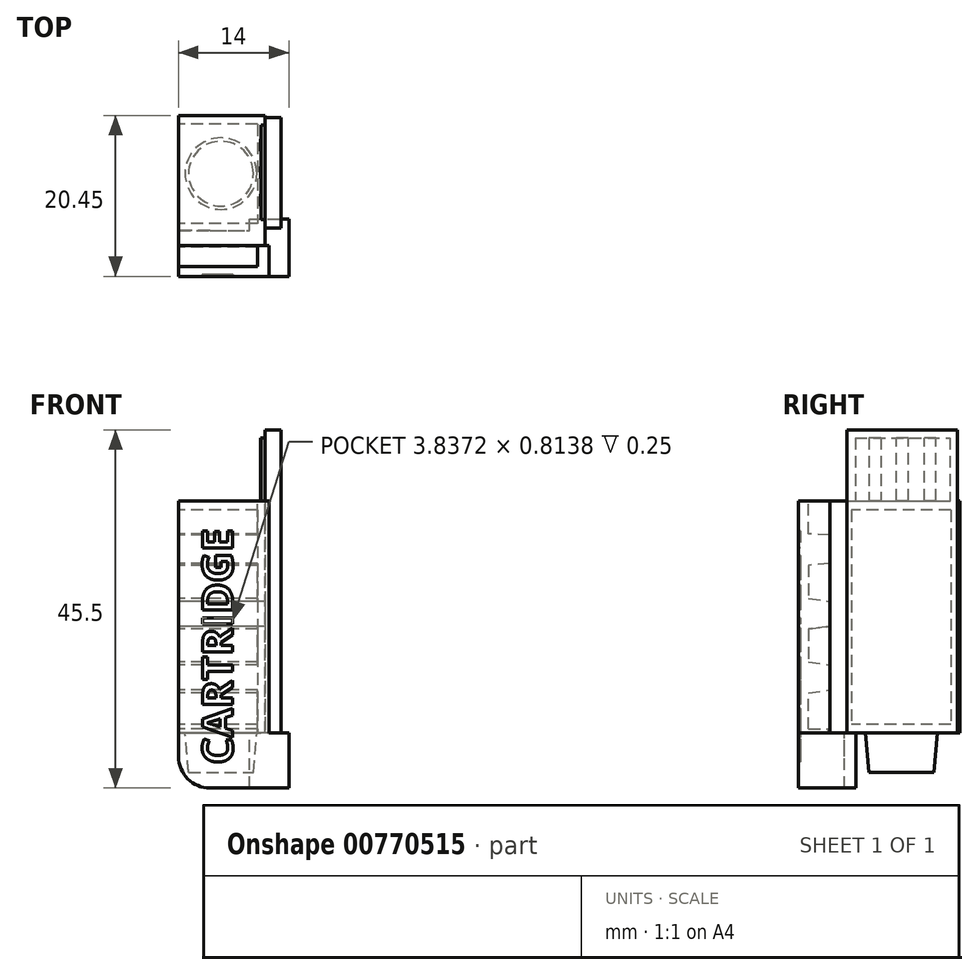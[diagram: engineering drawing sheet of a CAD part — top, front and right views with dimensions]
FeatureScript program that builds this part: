
annotation { "Feature Type Name" : "Feature", "Feature Type Description" : "" }
export const myFeature = defineFeature(function(context is Context, id is Id, definition is map)
    precondition{}
    {
        {
            var Q0;
            Q0=qCreatedBy(makeId("Right.planeOp"),FACE);
            var sketch = newSketch(context, id + "F0", { "sketchPlane" : qUnion([Q0])});
            skLineSegment(sketch, "E0", {"start": v(-7.8, 44.5) * mm, "end": v(-7.8, 0) * mm});
            skLineSegment(sketch, "E1", {"start": v(-7.8, 0) * mm, "end": v(0, 0) * mm});
            skLineSegment(sketch, "E2", {"start": v(0, 0) * mm, "end": v(0, 7) * mm});
            skLineSegment(sketch, "E3", {"start": v(0, 7) * mm, "end": v(-4.55, 7) * mm});
            skLineSegment(sketch, "E4", {"start": v(-5.05, 7.5) * mm, "end": v(-7.05, 7.5) * mm});
            skLineSegment(sketch, "E5", {"start": v(-7.05, 7.5) * mm, "end": v(-7.05, 12.1) * mm});
            skLineSegment(sketch, "E6", {"start": v(-4.35, 12.45) * mm, "end": v(-4.35, 15.65) * mm});
            skLineSegment(sketch, "E7", {"start": v(-7.05, 16) * mm, "end": v(-7.05, 20.2) * mm});
            skLineSegment(sketch, "E8", {"start": v(-4.35, 20.53) * mm, "end": v(-4.35, 23.73) * mm});
            skLineSegment(sketch, "E9", {"start": v(-7.05, 24.1) * mm, "end": v(-7.05, 28.3) * mm});
            skLineSegment(sketch, "E10", {"start": v(-7.05, 32.3) * mm, "end": v(-7.05, 36.5) * mm});
            skLineSegment(sketch, "E11", {"start": v(-7.05, 36.5) * mm, "end": v(-2.8, 36.5) * mm});
            skLineSegment(sketch, "E12", {"start": v(-4.55, 7) * mm, "end": v(-7.8, 7) * mm});
            skLineSegment(sketch, "E13", {"start": v(-5.05, 7.5) * mm, "end": v(-4.55, 7.5) * mm});
            skLineSegment(sketch, "E14", {"start": v(-4.55, 7.5) * mm, "end": v(-4.55, 7) * mm});
            skLineSegment(sketch, "E15", {"start": v(-2.8, 36.5) * mm, "end": v(-2.8, 44.5) * mm});
            skLineSegment(sketch, "E16", {"start": v(-2.8, 44.5) * mm, "end": v(-7.8, 44.5) * mm});
            skLineSegment(sketch, "E17", {"start": v(-4.35, 32.13) * mm, "end": v(-7.05, 32.3) * mm});
            skLineSegment(sketch, "E18", {"start": v(-4.35, 28.53) * mm, "end": v(-7.05, 28.3) * mm});
            skLineSegment(sketch, "E19", {"start": v(-4.35, 32.13) * mm, "end": v(-4.35, 28.53) * mm});
            skLineSegment(sketch, "E20", {"start": v(-7.05, 24.1) * mm, "end": v(-4.35, 23.73) * mm});
            skLineSegment(sketch, "E21", {"start": v(-7.05, 20.2) * mm, "end": v(-4.35, 20.53) * mm});
            skLineSegment(sketch, "E22", {"start": v(-7.05, 12.1) * mm, "end": v(-4.35, 12.45) * mm});
            skLineSegment(sketch, "E23", {"start": v(-4.35, 15.65) * mm, "end": v(-7.05, 16) * mm});
            skSolve(sketch);
        }
        {
            var Q0;
            Q0=makeQuery(id+"F0.imprint","IMPRINT",FACE,{"disambiguationData":[TD([[makeQuery(id+"F0.imprint","IMPRINT",EDGE,{"derivedFrom":sQuery(id+"F0.wireOp",EDGE,"E4")}),1.0]])]});
            extrude(context, id + "F1", {"entities" : qUnion([Q0]), "depth" : 10 * mm, "offsetDistance" : 25 * mm});
        }
        {
            var Q0;
            {var subQ0=sQuery(id+"F0.wireOp",EDGE,"E1");Q0=makeQuery(id+"F0.imprint","IMPRINT",FACE,{"disambiguationData":[TD([[makeQuery(id+"F0.imprint","IMPRINT",EDGE,{"derivedFrom":subQ0}),1.0]])]});}
            extrude(context, id + "F2", {"entities" : qUnion([Q0]), "operationType" : NewBodyOperationType.ADD, "depth" : 14 * mm});
        }
        {
            var Q0;
            Q0=makeQuery(id+"F0.imprint","IMPRINT",FACE,{"disambiguationData":[TD([[makeQuery(id+"F0.imprint","IMPRINT",EDGE,{"derivedFrom":sQuery(id+"F0.wireOp",EDGE,"E4")}),1.0]])]});
            var sketch = newSketch(context, id + "F3", { "sketchPlane" : qUnion([Q0])});
            skLineSegment(sketch, "E24.bottom", {"start": v(-2.8, 44.5) * mm, "end": v(-7.8, 44.5) * mm});
            skLineSegment(sketch, "E24.top", {"start": v(-2.8, 0) * mm, "end": v(-7.8, 0) * mm});
            skLineSegment(sketch, "E24.left", {"start": v(-2.8, 44.5) * mm, "end": v(-2.8, 0) * mm});
            skLineSegment(sketch, "E24.right", {"start": v(-7.8, 44.5) * mm, "end": v(-7.8, 0) * mm});
            skSolve(sketch);
        }
        {
            var Q0;
            Q0=makeQuery(id+"F1.opExtrude","CAP_FACE",FACE,{"disambiguationData":[OSD([sQuery(id+"F0.wireOp",EDGE,"E0"),sQuery(id+"F0.wireOp",EDGE,"E4"),sQuery(id+"F0.wireOp",EDGE,"E5"),sQuery(id+"F0.wireOp",EDGE,"E6"),sQuery(id+"F0.wireOp",EDGE,"E7"),sQuery(id+"F0.wireOp",EDGE,"E8"),sQuery(id+"F0.wireOp",EDGE,"E9"),sQuery(id+"F0.wireOp",EDGE,"E10"),sQuery(id+"F0.wireOp",EDGE,"E11"),sQuery(id+"F0.wireOp",EDGE,"E12"),sQuery(id+"F0.wireOp",EDGE,"E13"),sQuery(id+"F0.wireOp",EDGE,"E14"),sQuery(id+"F0.wireOp",EDGE,"E15"),sQuery(id+"F0.wireOp",EDGE,"E16"),sQuery(id+"F0.wireOp",EDGE,"E17"),sQuery(id+"F0.wireOp",EDGE,"E18"),sQuery(id+"F0.wireOp",EDGE,"E19"),sQuery(id+"F0.wireOp",EDGE,"E20"),sQuery(id+"F0.wireOp",EDGE,"E21"),sQuery(id+"F0.wireOp",EDGE,"E22"),sQuery(id+"F0.wireOp",EDGE,"E23")])],"isStart":false});
            var sketch = newSketch(context, id + "F4", { "sketchPlane" : qUnion([Q0])});
            skLineSegment(sketch, "E25.bottom", {"start": v(-7.8, 44.5) * mm, "end": v(-4.35, 44.5) * mm});
            skLineSegment(sketch, "E25.top", {"start": v(-7.8, 7) * mm, "end": v(-4.35, 7) * mm});
            skLineSegment(sketch, "E25.left", {"start": v(-7.8, 44.5) * mm, "end": v(-7.8, 7) * mm});
            skLineSegment(sketch, "E25.right", {"start": v(-4.35, 44.5) * mm, "end": v(-4.35, 7) * mm});
            skSolve(sketch);
        }
        {
            var Q0;
            Q0=qSketchRegion(id+"F4",true);
            extrude(context, id + "F5", {"entities" : qUnion([Q0]), "operationType" : NewBodyOperationType.ADD, "depth" : 1.5 * mm, "offsetDistance" : 25 * mm});
        }
        {
            var Q0;
            Q0=makeQuery(id+"F1.opExtrude","CAP_EDGE",EDGE,{"disambiguationData":[OSD([sQuery(id+"F0.wireOp",EDGE,"E16")])],"isStart":true});
            var Q1;
            Q1=makeQuery(id+"F2.opExtrude","CAP_EDGE",EDGE,{"disambiguationData":[OSD([sQuery(id+"F0.wireOp",EDGE,"E1")])],"isStart":true});
            fillet(context, id + "F6", {"entities" : qUnion([Q0, Q1]), "radius" : 4 * mm, "tangentPropagation" : true, "allowEdgeOverflow" : false});
        }
        {
            var Q0;
            Q0=makeQuery(id+"F1.opExtrude","SWEPT_FACE",FACE,{"disambiguationData":[OSD([sQuery(id+"F0.wireOp",EDGE,"E15")])]});
            var sketch = newSketch(context, id + "F7", { "sketchPlane" : qUnion([Q0])});
            skLineSegment(sketch, "E26.bottom", {"start": v(-11.5, 36.5) * mm, "end": v(0, 36.5) * mm});
            skLineSegment(sketch, "E26.top", {"start": v(-11.5, 44.5) * mm, "end": v(0, 44.5) * mm});
            skLineSegment(sketch, "E26.left", {"start": v(0, 36.5) * mm, "end": v(0, 44.5) * mm});
            skLineSegment(sketch, "E26.right", {"start": v(-11.5, 36.5) * mm, "end": v(-11.5, 44.5) * mm});
            skSolve(sketch);
        }
        {
            var Q0;
            Q0=qSketchRegion(id+"F7",true);
            extrude(context, id + "F8", {"entities" : qUnion([Q0]), "operationType" : NewBodyOperationType.REMOVE, "oppositeDirection" : true, "depth" : 25 * mm, "offsetDistance" : 25 * mm});
        }
        {
            var Q0;
            Q0=makeQuery(id+"F2.opExtrude","CAP_FACE",FACE,{"disambiguationData":[OSD([sQuery(id+"F0.wireOp",EDGE,"E0"),sQuery(id+"F0.wireOp",EDGE,"E1"),sQuery(id+"F0.wireOp",EDGE,"E2"),sQuery(id+"F0.wireOp",EDGE,"E3"),sQuery(id+"F0.wireOp",EDGE,"E12")])],"isStart":false});
            var sketch = newSketch(context, id + "F9", { "sketchPlane" : qUnion([Q0])});
            skLineSegment(sketch, "E27.bottom", {"start": v(0, 0) * mm, "end": v(-1, 0) * mm});
            skLineSegment(sketch, "E27.top", {"start": v(0, 7) * mm, "end": v(-1, 7) * mm});
            skLineSegment(sketch, "E27.left", {"start": v(0, 0) * mm, "end": v(0, 7) * mm});
            skLineSegment(sketch, "E27.right", {"start": v(-1, 0) * mm, "end": v(-1, 7) * mm});
            skSolve(sketch);
        }
        {
            var Q0;
            Q0=qSketchRegion(id+"F9",true);
            extrude(context, id + "F10", {"entities" : qUnion([Q0]), "operationType" : NewBodyOperationType.REMOVE, "endBound" : BoundingType.THROUGH_ALL, "oppositeDirection" : true, "depth" : 25 * mm, "offsetDistance" : 25 * mm});
        }
        {
            var Q0;
            {var subQ0=sQuery(id+"F0.wireOp",EDGE,"E0");Q0=makeQuery(id+"F5.boolean.opBoolean","MERGE",FACE,{"derivedFrom":[makeQuery(id+"F2.boolean.opBoolean","MERGE",FACE,{"derivedFrom":[makeQuery(id+"F1.opExtrude","SWEPT_FACE",FACE,{"disambiguationData":[OSD([subQ0])]}),makeQuery(id+"F2.opExtrude","SWEPT_FACE",FACE,{"disambiguationData":[OSD([subQ0])]})]}),makeQuery(id+"F5.opExtrude","SWEPT_FACE",FACE,{"disambiguationData":[OSD([sQuery(id+"F4.wireOp",EDGE,"E25.left")])]})]});}
            var sketch = newSketch(context, id + "F11", { "sketchPlane" : qUnion([Q0])});
            skLineSegment(sketch, "E28", {"start": v(0, 36.5) * mm, "end": v(11.5, 36.5) * mm});
            skLineSegment(sketch, "E29", {"start": v(11.5, 36.5) * mm, "end": v(11.5, 7) * mm});
            skLineSegment(sketch, "E30", {"start": v(11.5, 7) * mm, "end": v(14, 7) * mm});
            skLineSegment(sketch, "E31", {"start": v(14, 7) * mm, "end": v(14, 0) * mm});
            skLineSegment(sketch, "E32", {"start": v(14, 0) * mm, "end": v(4, 0) * mm});
            skLineSegment(sketch, "E33", {"start": v(0, 4) * mm, "end": v(0, 36.5) * mm});
            skArc(sketch, "E34.filletArc", {"start": v(0, 4) * mm, "mid": v(1.17, 1.17) * mm, "end": v(4, 0) * mm});
            skSolve(sketch);
        }
        {
            var Q0;
            Q0=qSketchRegion(id+"F11",true);
            extrude(context, id + "F12", {"entities" : qUnion([Q0]), "operationType" : NewBodyOperationType.ADD, "depth" : 0.5 * mm, "offsetDistance" : 25 * mm});
        }
        {
            var Q0;
            Q0=makeQuery(id+"F10.boolean.opBoolean","COPY",FACE,{"derivedFrom":makeQuery(id+"F10.opExtrude","SWEPT_FACE",FACE,{"disambiguationData":[OSD([sQuery(id+"F9.wireOp",EDGE,"E27.right")])]})});
            var sketch = newSketch(context, id + "F13", { "sketchPlane" : qUnion([Q0])});
            skLineSegment(sketch, "E35.bottom", {"start": v(0, 0) * mm, "end": v(0, 7) * mm});
            skLineSegment(sketch, "E35.top", {"start": v(-9, 0) * mm, "end": v(-9, 7) * mm});
            skLineSegment(sketch, "E35.left", {"start": v(0, 0) * mm, "end": v(-9, 0) * mm});
            skLineSegment(sketch, "E35.right", {"start": v(0, 7) * mm, "end": v(-9, 7) * mm});
            skSolve(sketch);
        }
        {
            var Q0;
            Q0=qSketchRegion(id+"F13",true);
            extrude(context, id + "F14", {"entities" : qUnion([Q0]), "operationType" : NewBodyOperationType.REMOVE, "oppositeDirection" : true, "depth" : 1.5 * mm, "offsetDistance" : 25 * mm});
        }
        {
            var Q0;
            Q0=makeQuery(id+"F12.opExtrude","CAP_FACE",FACE,{"disambiguationData":[OSD([sQuery(id+"F11.wireOp",EDGE,"E28"),sQuery(id+"F11.wireOp",EDGE,"E29"),sQuery(id+"F11.wireOp",EDGE,"E30"),sQuery(id+"F11.wireOp",EDGE,"E31"),sQuery(id+"F11.wireOp",EDGE,"E32"),sQuery(id+"F11.wireOp",EDGE,"E33"),sQuery(id+"F11.wireOp",EDGE,"E34.filletArc")])],"isStart":false});
            var sketch = newSketch(context, id + "F15", { "sketchPlane" : qUnion([Q0])});
            skText(sketch, "E36", { "text": "CARTRIDGE", "fontName": "OpenSans-Bold.ttf"});
            const initialGuessF15  = {"E36": [0.00687, 0.003, 0, 1, 0.00387]};
            skSetInitialGuess(sketch, initialGuessF15);
            skSolve(sketch);
        }
        {
            var Q0;
            Q0=qSketchRegion(id+"F15",true);
            extrude(context, id + "F16", {"entities" : qUnion([Q0]), "operationType" : NewBodyOperationType.REMOVE, "oppositeDirection" : true, "depth" : 0.25 * mm, "offsetDistance" : 25 * mm});
        }
        {
            var Q0;
            Q0=qCreatedBy(makeId("Right.planeOp"),FACE);
            var sketch = newSketch(context, id + "F17", { "sketchPlane" : qUnion([Q0])});
            skLineSegment(sketch, "E37", {"start": v(-7.05, 36.5) * mm, "end": v(12.15, 36.5) * mm});
            skLineSegment(sketch, "E38", {"start": v(12.15, 36.5) * mm, "end": v(12.15, 7) * mm});
            skLineSegment(sketch, "E39", {"start": v(-7.05, 36.5) * mm, "end": v(-7.05, 32.3) * mm});
            skLineSegment(sketch, "E40", {"start": v(-7.05, 32.3) * mm, "end": v(-4.35, 32.13) * mm});
            skLineSegment(sketch, "E41", {"start": v(-4.35, 32.13) * mm, "end": v(-4.35, 28.53) * mm});
            skLineSegment(sketch, "E42", {"start": v(-4.35, 28.53) * mm, "end": v(-7.05, 28.3) * mm});
            skLineSegment(sketch, "E43", {"start": v(-7.05, 28.3) * mm, "end": v(-7.05, 24.1) * mm});
            skLineSegment(sketch, "E44", {"start": v(-7.05, 24.1) * mm, "end": v(-4.35, 23.73) * mm});
            skLineSegment(sketch, "E45", {"start": v(-4.35, 23.73) * mm, "end": v(-4.35, 20.53) * mm});
            skLineSegment(sketch, "E46", {"start": v(-4.35, 20.53) * mm, "end": v(-7.05, 20.2) * mm});
            skLineSegment(sketch, "E47", {"start": v(-7.05, 20.2) * mm, "end": v(-7.05, 16) * mm});
            skLineSegment(sketch, "E48", {"start": v(-7.05, 16) * mm, "end": v(-4.35, 15.65) * mm});
            skLineSegment(sketch, "E49", {"start": v(-4.35, 15.65) * mm, "end": v(-4.35, 12.45) * mm});
            skLineSegment(sketch, "E50", {"start": v(-4.35, 12.45) * mm, "end": v(-7.05, 12.1) * mm});
            skLineSegment(sketch, "E51", {"start": v(-7.05, 12.1) * mm, "end": v(-7.05, 7.5) * mm});
            skLineSegment(sketch, "E52", {"start": v(-4.35, 36.5) * mm, "end": v(-4.35, 7) * mm});
            skPoint(sketch, "E52.startSnap0", {"position": v(-4.35, 30.33) * mm});
            skLineSegment(sketch, "E53", {"start": v(-4.55, 7.5) * mm, "end": v(-4.55, 7) * mm});
            skLineSegment(sketch, "E54", {"start": v(-4.55, 7) * mm, "end": v(12.15, 7) * mm});
            skLineSegment(sketch, "E55", {"start": v(-4.55, 7.5) * mm, "end": v(-7.05, 7.5) * mm});
            skSolve(sketch);
        }
        {
            var Q0;
            {var subQ12=sQuery(id+"F17.wireOp",EDGE,"E38");Q0=makeQuery(id+"F17.imprint","IMPRINT",FACE,{"disambiguationData":[TD([[makeQuery(id+"F17.imprint","IMPRINT",EDGE,{"derivedFrom":subQ12}),-1.0]])]});}
            extrude(context, id + "F18", {"entities" : qUnion([Q0]), "depth" : 11 * mm, "offsetDistance" : 25 * mm});
        }
        {
            var Q0;
            {var subQ0=sQuery(id+"F17.wireOp",EDGE,"E39");Q0=makeQuery(id+"F17.imprint","IMPRINT",FACE,{"disambiguationData":[TD([[makeQuery(id+"F17.imprint","IMPRINT",EDGE,{"derivedFrom":subQ0}),1.0]])]});}
            var Q1;
            {var subQ0=sQuery(id+"F17.wireOp",EDGE,"E42");Q1=makeQuery(id+"F17.imprint","IMPRINT",FACE,{"disambiguationData":[TD([[makeQuery(id+"F17.imprint","IMPRINT",EDGE,{"derivedFrom":subQ0}),1.0]])]});}
            var Q2;
            {var subQ0=sQuery(id+"F17.wireOp",EDGE,"E47");Q2=makeQuery(id+"F17.imprint","IMPRINT",FACE,{"disambiguationData":[TD([[makeQuery(id+"F17.imprint","IMPRINT",EDGE,{"derivedFrom":subQ0}),1.0]])]});}
            var Q3;
            {var subQ2=sQuery(id+"F17.wireOp",EDGE,"E50");Q3=makeQuery(id+"F17.imprint","IMPRINT",FACE,{"disambiguationData":[TD([[makeQuery(id+"F17.imprint","IMPRINT",EDGE,{"derivedFrom":subQ2}),1.0]])]});}
            extrude(context, id + "F19", {"entities" : qUnion([Q0, Q1, Q2, Q3]), "depth" : 10 * mm, "offsetDistance" : 25 * mm});
        }
        {
            var Q0;
            Q0=makeQuery(id+"F18.opExtrude","SWEPT_FACE",FACE,{"disambiguationData":[OSD([sQuery(id+"F17.wireOp",EDGE,"E54")])]});
            var sketch = newSketch(context, id + "F20", { "sketchPlane" : qUnion([Q0])});
            skCircle(sketch, "E56", {"center": v(5.38, -4.76) * mm, "radius": 4.55 * mm});
            skSolve(sketch);
        }
        {
            var Q0;
            Q0=makeQuery(id+"F20.imprint","IMPRINT",FACE,{"disambiguationData":[TD([[makeQuery(id+"F20.imprint","IMPRINT",EDGE,{"derivedFrom":sQuery(id+"F20.wireOp",EDGE,"E56")}),1.0]])]});
            extrude(context, id + "F21", {"entities" : qUnion([Q0]), "depth" : 5 * mm, "offsetDistance" : 25 * mm, "hasDraft" : true, "draftAngle" : 5 * degree, "draftPullDirection" : true});
        }
        {
            var Q0;
            Q0=makeQuery(id+"F18.opExtrude","SWEPT_FACE",FACE,{"disambiguationData":[OSD([sQuery(id+"F17.wireOp",EDGE,"E37")])]});
            var sketch = newSketch(context, id + "F22", { "sketchPlane" : qUnion([Q0])});
            skLineSegment(sketch, "E57.bottom", {"start": v(11, 10.9) * mm, "end": v(10.5, 10.9) * mm});
            skLineSegment(sketch, "E57.top", {"start": v(11, -1.1) * mm, "end": v(10.5, -1.1) * mm});
            skLineSegment(sketch, "E57.left", {"start": v(11, 10.9) * mm, "end": v(11, -1.1) * mm});
            skLineSegment(sketch, "E57.right", {"start": v(10.5, 10.9) * mm, "end": v(10.5, -1.1) * mm});
            skSolve(sketch);
        }
        {
            var Q0;
            Q0=makeQuery(id+"F22.imprint","IMPRINT",FACE,{"disambiguationData":[TD([[makeQuery(id+"F22.imprint","IMPRINT",EDGE,{"derivedFrom":sQuery(id+"F22.wireOp",EDGE,"E57.bottom")}),1.0]])]});
            extrude(context, id + "F23", {"entities" : qUnion([Q0]), "depth" : 8 * mm, "offsetDistance" : 25 * mm});
        }
        {
            var Q0;
            Q0=makeQuery(id+"F23.opExtrude","SWEPT_FACE",FACE,{"disambiguationData":[OSD([sQuery(id+"F22.wireOp",EDGE,"E57.right")])]});
            var sketch = newSketch(context, id + "F24", { "sketchPlane" : qUnion([Q0])});
            skLineSegment(sketch, "E58.bottom", {"start": v(-0.65, 44.5) * mm, "end": v(-2.15, 44.5) * mm});
            skLineSegment(sketch, "E58.top", {"start": v(-0.65, 36.5) * mm, "end": v(-2.15, 36.5) * mm});
            skLineSegment(sketch, "E58.left", {"start": v(-0.65, 44.5) * mm, "end": v(-0.65, 36.5) * mm});
            skLineSegment(sketch, "E58.right", {"start": v(-2.15, 44.5) * mm, "end": v(-2.15, 36.5) * mm});
            skLineSegment(sketch, "E59.bottom", {"start": v(-4.15, 36.5) * mm, "end": v(-5.65, 36.5) * mm});
            skLineSegment(sketch, "E59.top", {"start": v(-4.15, 44.5) * mm, "end": v(-5.65, 44.5) * mm});
            skLineSegment(sketch, "E59.left", {"start": v(-4.15, 36.5) * mm, "end": v(-4.15, 44.5) * mm});
            skLineSegment(sketch, "E59.right", {"start": v(-5.65, 36.5) * mm, "end": v(-5.65, 44.5) * mm});
            skLineSegment(sketch, "E60.bottom", {"start": v(-7.65, 36.5) * mm, "end": v(-9.15, 36.5) * mm});
            skLineSegment(sketch, "E60.top", {"start": v(-7.65, 44.5) * mm, "end": v(-9.15, 44.5) * mm});
            skLineSegment(sketch, "E60.left", {"start": v(-7.65, 36.5) * mm, "end": v(-7.65, 44.5) * mm});
            skLineSegment(sketch, "E60.right", {"start": v(-9.15, 36.5) * mm, "end": v(-9.15, 44.5) * mm});
            skSolve(sketch);
        }
        {
            var Q0;
            Q0 = qSketchRegion(id + "F24", true);
            extrude(context, id + "F25", {"entities" : qUnion([Q0]), "depth" : 0.1 * mm, "offsetDistance" : 25 * mm});
        }
        {
            var Q0;
            Q0=makeQuery(id+"F18.opExtrude","CAP_FACE",FACE,{"disambiguationData":[OSD([sQuery(id+"F17.wireOp",EDGE,"E37"),sQuery(id+"F17.wireOp",EDGE,"E38"),sQuery(id+"F17.wireOp",EDGE,"E44"),sQuery(id+"F17.wireOp",EDGE,"E45"),sQuery(id+"F17.wireOp",EDGE,"E46"),sQuery(id+"F17.wireOp",EDGE,"E52"),sQuery(id+"F17.wireOp",EDGE,"E54")])],"isStart":false});
            var sketch = newSketch(context, id + "F26", { "sketchPlane" : qUnion([Q0])});
            skLineSegment(sketch, "E61.bottom", {"start": v(-2.15, 7) * mm, "end": v(11.85, 7) * mm});
            skLineSegment(sketch, "E61.top", {"start": v(-2.15, 45.5) * mm, "end": v(11.85, 45.5) * mm});
            skLineSegment(sketch, "E61.left", {"start": v(-2.15, 7) * mm, "end": v(-2.15, 45.5) * mm});
            skLineSegment(sketch, "E61.right", {"start": v(11.85, 7) * mm, "end": v(11.85, 45.5) * mm});
            skSolve(sketch);
        }
        {
            var Q0;
            Q0 = qSketchRegion(id + "F26", true);
            var Q1;
            Q1=sQuery(id+"F26.wireOp",EDGE,"E61.top");
            extrude(context, id + "F27", {"entities" : qUnion([Q0]), "surfaceEntities" : qUnion([Q1]), "depth" : 2 * mm, "offsetDistance" : 25 * mm});
        }
        {
            var Q0;
            {var subQ12=sQuery(id+"F17.wireOp",EDGE,"E38");Q0=makeQuery(id+"F17.imprint","IMPRINT",FACE,{"disambiguationData":[TD([[makeQuery(id+"F17.imprint","IMPRINT",EDGE,{"derivedFrom":subQ12}),-1.0]])]});}
            var sketch = newSketch(context, id + "F28", { "sketchPlane" : qUnion([Q0])});
            skLineSegment(sketch, "E62.bottom", {"start": v(11.03, 35.31) * mm, "end": v(-1.57, 35.31) * mm});
            skLineSegment(sketch, "E62.top", {"start": v(11.03, 8.1) * mm, "end": v(-1.57, 8.1) * mm});
            skLineSegment(sketch, "E62.left", {"start": v(11.03, 35.31) * mm, "end": v(11.03, 8.1) * mm});
            skLineSegment(sketch, "E62.right", {"start": v(-1.57, 35.31) * mm, "end": v(-1.57, 8.1) * mm});
            skSolve(sketch);
        }
        {
            var Q0;
            Q0=makeQuery(id+"F28.imprint","IMPRINT",FACE,{"disambiguationData":[TD([[makeQuery(id+"F28.imprint","IMPRINT",EDGE,{"derivedFrom":sQuery(id+"F28.wireOp",EDGE,"E62.bottom")}),1.0]])]});
            extrude(context, id + "F29", {"entities" : qUnion([Q0]), "operationType" : NewBodyOperationType.REMOVE, "depth" : 10 * mm, "offsetDistance" : 25 * mm});
        }
        {
            var Q0;
            {var subQ12=sQuery(id+"F17.wireOp",EDGE,"E38");Q0=makeQuery(id+"F17.imprint","IMPRINT",FACE,{"disambiguationData":[TD([[makeQuery(id+"F17.imprint","IMPRINT",EDGE,{"derivedFrom":subQ12}),-1.0]])]});}
            var sketch = newSketch(context, id + "F30", { "sketchPlane" : qUnion([Q0])});
            skLineSegment(sketch, "E63.bottom", {"start": v(11.03, 35.31) * mm, "end": v(-1.57, 35.31) * mm});
            skLineSegment(sketch, "E63.top", {"start": v(11.03, 8.1) * mm, "end": v(-1.57, 8.1) * mm});
            skLineSegment(sketch, "E63.left", {"start": v(11.03, 35.31) * mm, "end": v(11.03, 8.1) * mm});
            skLineSegment(sketch, "E63.right", {"start": v(-1.57, 35.31) * mm, "end": v(-1.57, 8.1) * mm});
            skSolve(sketch);
        }
        {
            var Q0;
            Q0 = qSketchRegion(id + "F30", true);
            extrude(context, id + "F31", {"entities" : qUnion([Q0]), "depth" : 10 * mm, "offsetDistance" : 25 * mm});
        }
    });
